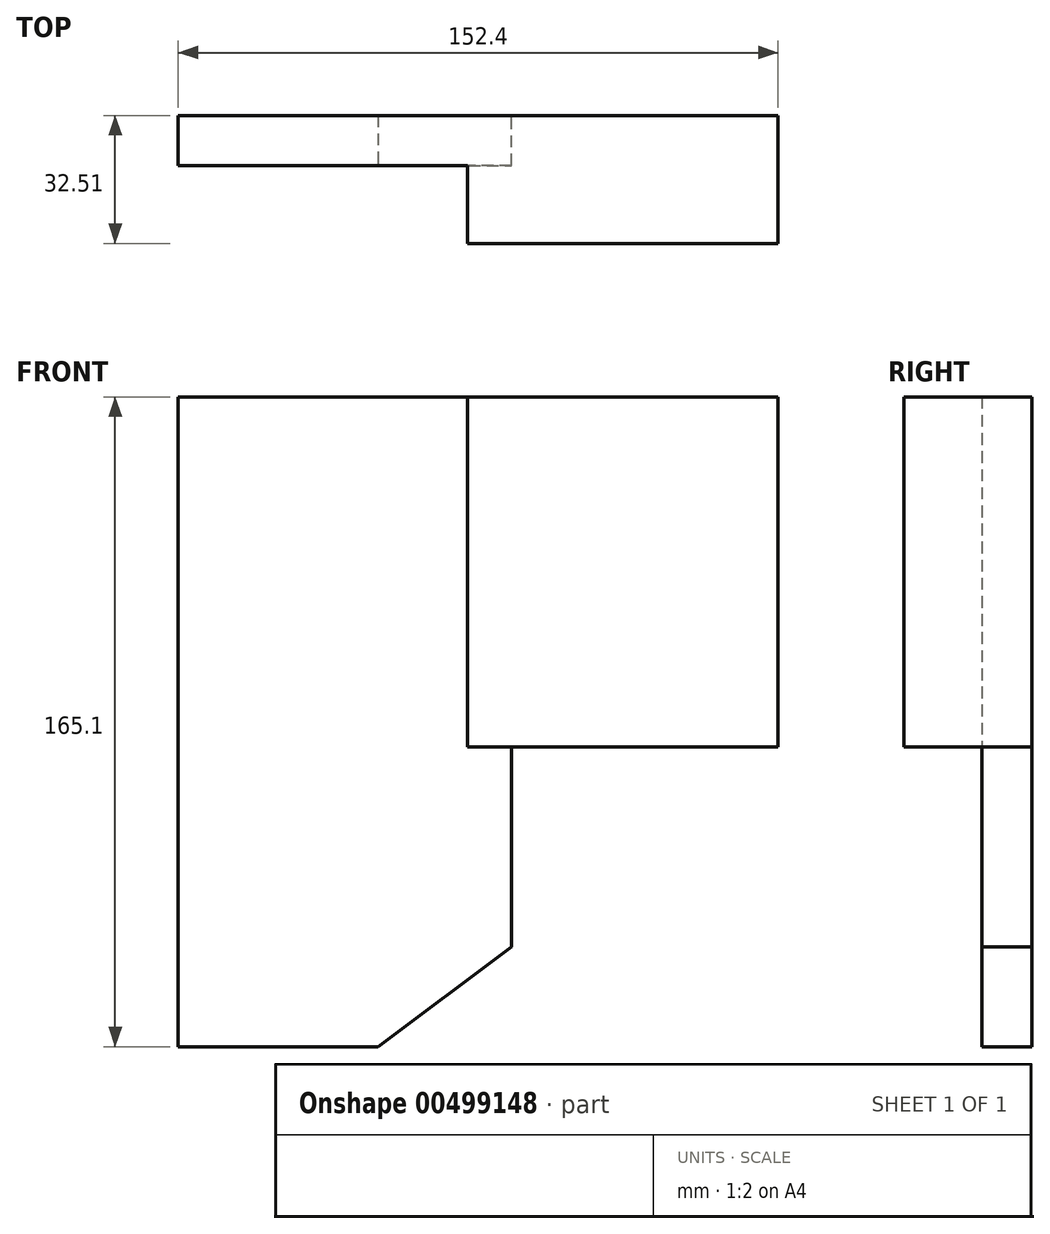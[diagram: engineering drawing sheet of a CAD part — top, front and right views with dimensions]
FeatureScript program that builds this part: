
annotation { "Feature Type Name" : "Feature", "Feature Type Description" : "" }
export const myFeature = defineFeature(function(context is Context, id is Id, definition is map)
    precondition{}
    {
        {
            var Q0;
            Q0=qCreatedBy(makeId("Top.planeOp"),FACE);
            var sketch = newSketch(context, id + "F0", { "sketchPlane" : qUnion([Q0])});
            skLineSegment(sketch, "E0.bottom", {"start": v(76.2, 6.35) * mm, "end": v(-76.2, 6.35) * mm});
            skLineSegment(sketch, "E0.top", {"start": v(76.2, -6.35) * mm, "end": v(-76.2, -6.35) * mm});
            skLineSegment(sketch, "E0.left", {"start": v(76.2, 6.35) * mm, "end": v(76.2, -6.35) * mm});
            skLineSegment(sketch, "E0.right", {"start": v(-76.2, 6.35) * mm, "end": v(-76.2, -6.35) * mm});
            skPoint(sketch, "E0.middle", {"position": v(0, 0) * mm});
            skSolve(sketch);
        }
        {
            var Q0;
            Q0=makeQuery(id+"F0.imprint","IMPRINT",FACE,{"disambiguationData":[TD([[makeQuery(id+"F0.imprint","IMPRINT",EDGE,{"derivedFrom":sQuery(id+"F0.wireOp",EDGE,"E0.bottom")}),1.0]])]});
            extrude(context, id + "F1", {"entities" : qUnion([Q0]), "depth" : 165.1 * mm});
        }
        {
            var Q0;
            Q0=makeQuery(id+"F1.opExtrude","CAP_EDGE",EDGE,{"disambiguationData":[OSD([sQuery(id+"F0.wireOp",EDGE,"E0.left")])],"isStart":true});
            chamfer(context, id + "F2", {"entities" : qUnion([Q0]), "chamferType" : ChamferType.TWO_OFFSETS, "width1" : 101.6 * mm, "oppositeDirection" : false, "width2" : 76.2 * mm, "tangentPropagation" : true});
        }
        {
            var Q0;
            Q0=makeQuery(id+"F1.opExtrude","SWEPT_FACE",FACE,{"disambiguationData":[OSD([sQuery(id+"F0.wireOp",EDGE,"E0.top")])]});
            var sketch = newSketch(context, id + "F3", { "sketchPlane" : qUnion([Q0])});
            skLineSegment(sketch, "E1.bottom", {"start": v(76.2, 165.1) * mm, "end": v(-2.72, 165.1) * mm});
            skLineSegment(sketch, "E1.top", {"start": v(76.2, 76.2) * mm, "end": v(-2.72, 76.2) * mm});
            skLineSegment(sketch, "E1.left", {"start": v(76.2, 165.1) * mm, "end": v(76.2, 76.2) * mm});
            skLineSegment(sketch, "E1.right", {"start": v(-2.72, 165.1) * mm, "end": v(-2.72, 76.2) * mm});
            skSolve(sketch);
        }
        {
            var Q0;
            Q0=makeQuery(id+"F3.imprint","IMPRINT",FACE,{"disambiguationData":[TD([[makeQuery(id+"F3.imprint","IMPRINT",EDGE,{"derivedFrom":sQuery(id+"F3.wireOp",EDGE,"E1.bottom")}),1.0]])]});
            extrude(context, id + "F4", {"entities" : qUnion([Q0]), "operationType" : NewBodyOperationType.ADD, "depth" : 19.8 * mm});
        }
        {
            var Q0;
            Q0=makeQuery(id+"F1.opExtrude","SWEPT_FACE",FACE,{"disambiguationData":[OSD([sQuery(id+"F0.wireOp",EDGE,"E0.bottom")])]});
            var sketch = newSketch(context, id + "F5", { "sketchPlane" : qUnion([Q0])});
            skLineSegment(sketch, "E2", {"start": v(-76.2, 76.2) * mm, "end": v(-8.47, 76.2) * mm});
            skLineSegment(sketch, "E3", {"start": v(-8.47, 76.2) * mm, "end": v(-8.47, 25.4) * mm});
            skLineSegment(sketch, "E4", {"start": v(-8.47, 25.4) * mm, "end": v(-76.2, 76.2) * mm});
            skSolve(sketch);
        }
        {
            var Q0;
            Q0=makeQuery(id+"F5.imprint","IMPRINT",FACE,{"disambiguationData":[TD([[makeQuery(id+"F5.imprint","IMPRINT",EDGE,{"derivedFrom":sQuery(id+"F5.wireOp",EDGE,"E2")}),-1.0]])]});
            extrude(context, id + "F6", {"entities" : qUnion([Q0]), "operationType" : NewBodyOperationType.REMOVE, "oppositeDirection" : true, "depth" : 25.4 * mm});
        }
    });
